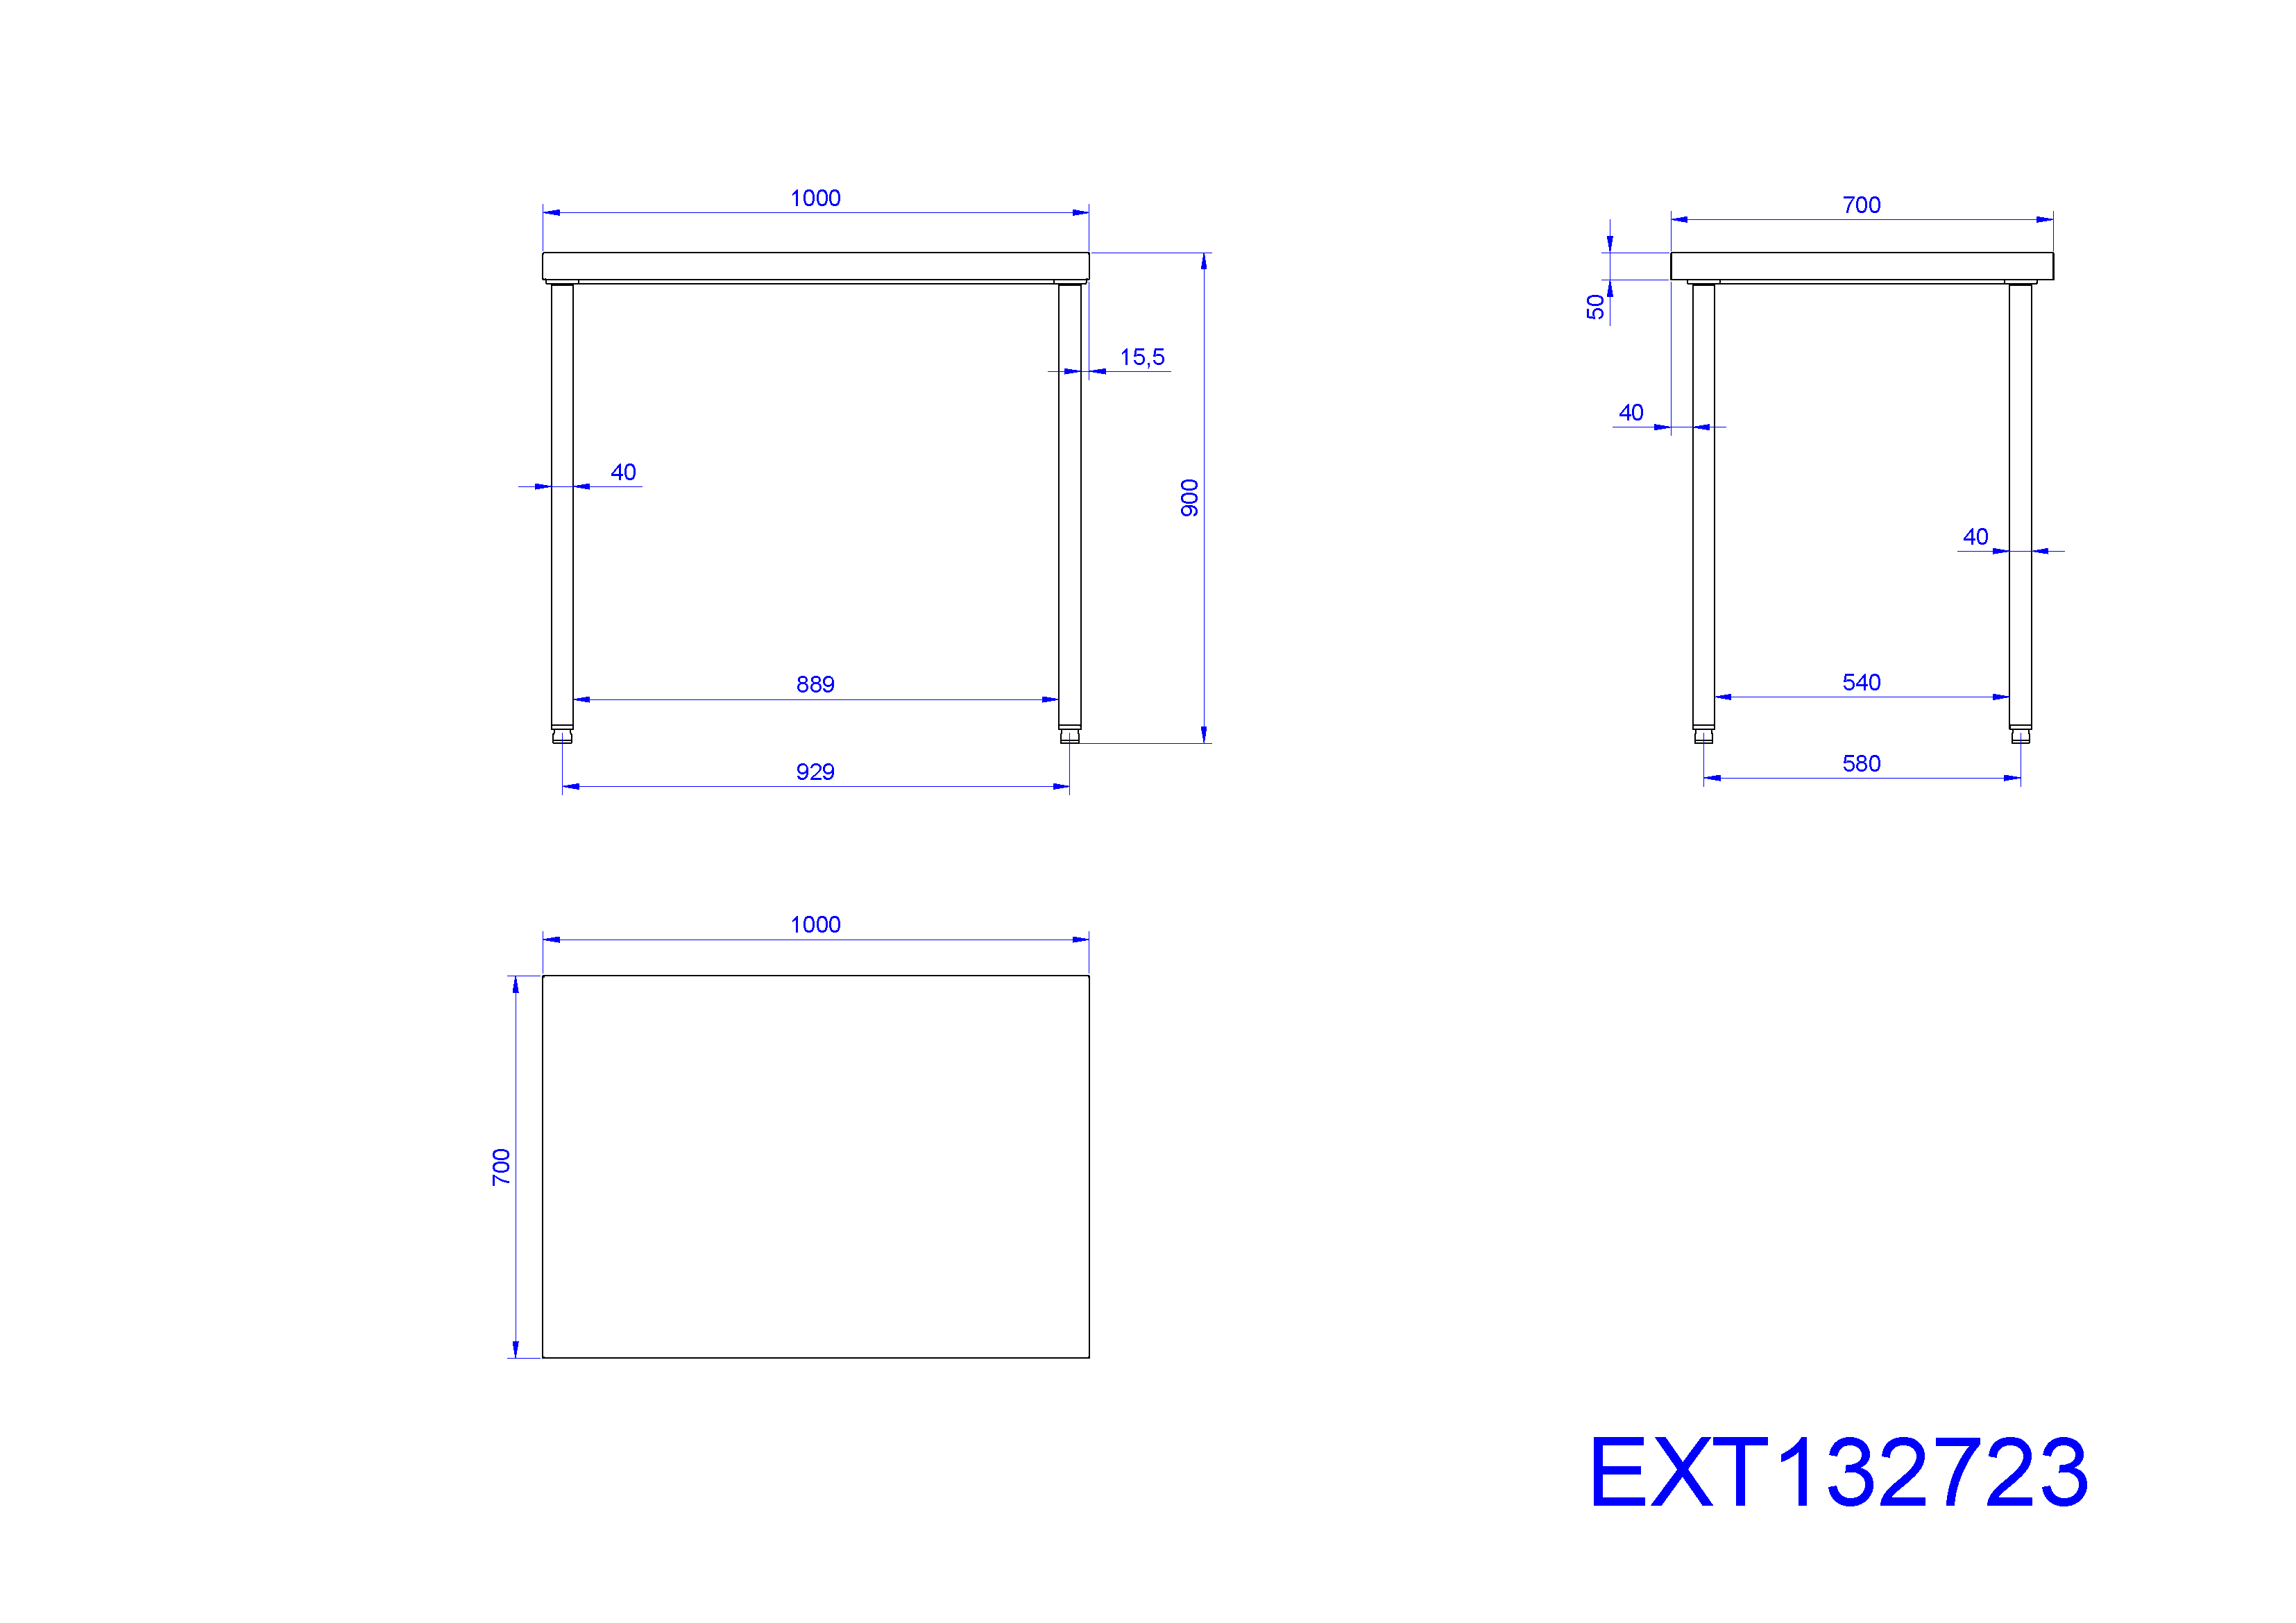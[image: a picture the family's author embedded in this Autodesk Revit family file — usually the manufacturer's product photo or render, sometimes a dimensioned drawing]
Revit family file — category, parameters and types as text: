
# Revit family: QF_ELECTROLUXPROFESSIONAL_132919_ML2S1817RN
name_source: partatom
category: Attrezzature speciali
units: mm (PartAtom-declared; Revit-internal decimal feet)

## family parameters
Basato su piano di lavoro = No
Condiviso = No
Punto di calcolo locali = No
Quota connettore circolare = Usa diametro
Sempre verticale = Sì
Taglio con vuoti quando caricato = No
Tipo di parte = Normale

## types (1)
- Standard
    Accessory = Sì
    Cold Water Size = 0 mm
    Compressed Air Pressure = 0.0 Pa
    Compressed Air Size = 0 mm
    Compressed Air Volume = 0.0 L/s
    Condensate Return Size = 0 mm
    Cycle = 0 Hz
    Depth Actual = 700 mm  [stored 2.29659 ft]
    Descrizione = CUPB.SINK 2 BOWLS(500X500)R/H DRAIN.1800
    Direct Waste Size = 140 mm
    Gas Input Pressure = 0
    Gas KW = 0
    Gas Size = 0 mm
    HP = 0 HP
    Height Actual = 1000 mm  [stored 3.28084 ft]
    Hot Water Size = 0 mm
    Item Number = 132919
    Length Actual = 1800 mm  [stored 5.90551 ft]
    Modello = ML2S1817RN
    Phase = 0
    Produttore = Electrolux Professional
    Prospetto di default = 0 mm  [stored 0 ft]
    Refrigerant Compressor Remote = Sì
    Refrigeration Liquid Line Size = 0 mm  [stored 0 ft]
    Refrigeration Suction Line Size = 0 mm  [stored 0 ft]
    Steam Consumption per Hour = 0
    Steam Supply Maximum Pressure = 0.0 Pa
    Steam Supply Minimum Pressure = 0.0 Pa
    Steam Supply Size = 0 mm
    URL = https://www.electroluxprofessional.com
    URL Manufacturer = https://www.electroluxprofessional.com
    Volts = 0 V
    Watts = 0 W
    Weight = 70.00 kg

note: source unit labels omitted for Gas Input Pressure — the stored unit's dimension contradicts the parameter name (converter mislabeling)

note: [stored X ft] marks values corroborated as IEEE doubles in the binary element streams (Revit-internal decimal feet)

## geometry (parser evidence)
native form markers: Blend x4, Sweep x4
no freeform markers — native parametric forms only
